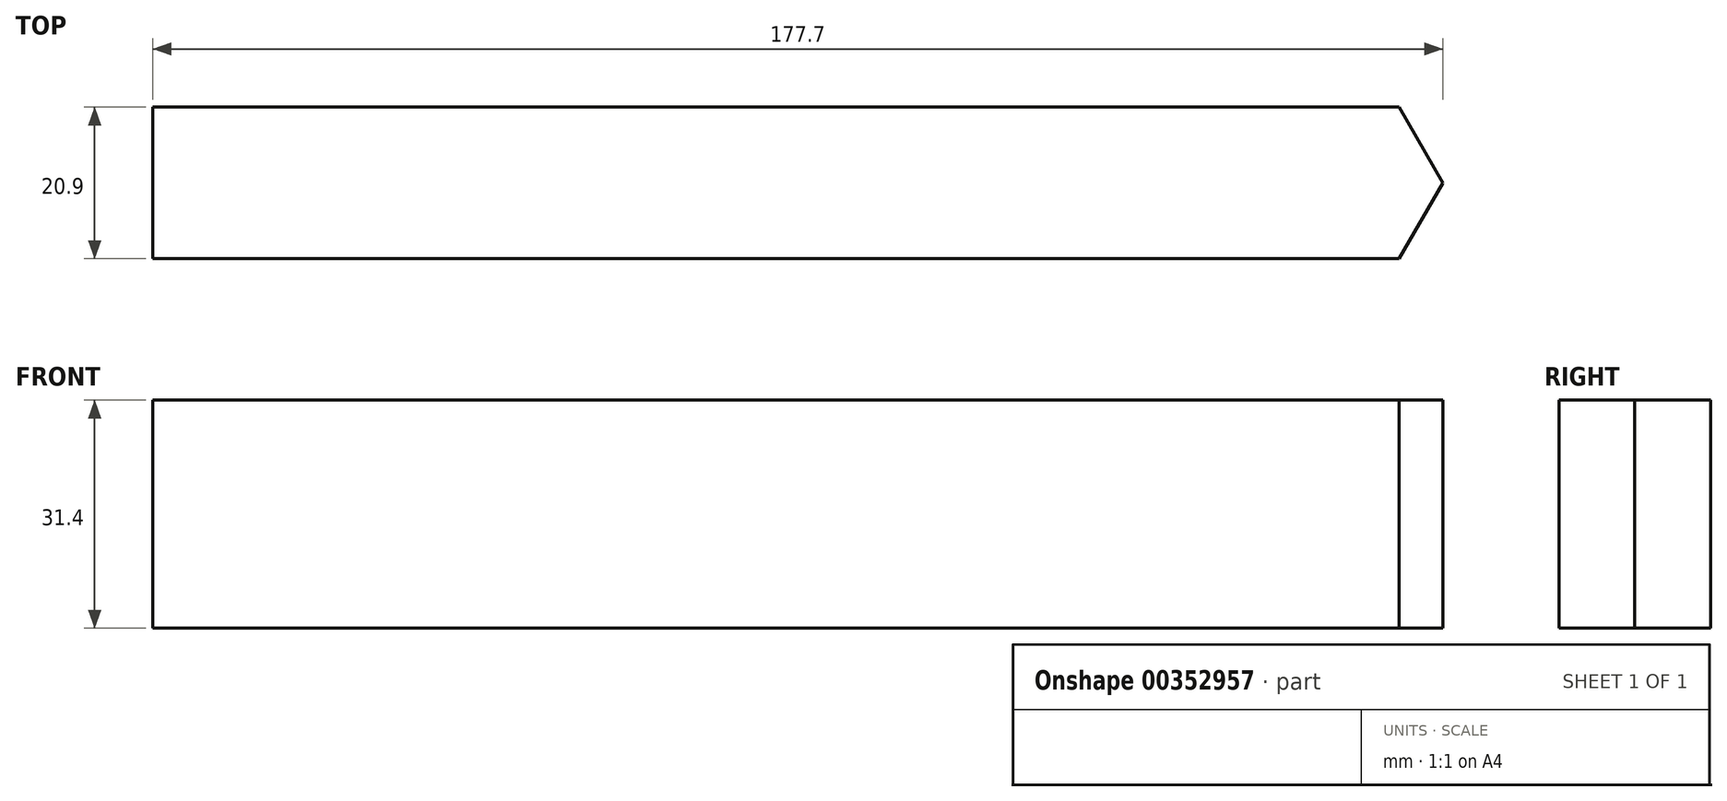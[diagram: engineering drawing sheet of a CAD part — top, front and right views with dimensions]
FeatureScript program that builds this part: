
annotation { "Feature Type Name" : "Feature", "Feature Type Description" : "" }
export const myFeature = defineFeature(function(context is Context, id is Id, definition is map)
    precondition{}
    {
        {
            var Q0;
            Q0=qCreatedBy(makeId("Top.planeOp"),FACE);
            var sketch = newSketch(context, id + "F0", { "sketchPlane" : qUnion([Q0])});
            skLineSegment(sketch, "E0.bottom", {"start": v(-132.89, -10.45) * mm, "end": v(38.81, -10.45) * mm});
            skLineSegment(sketch, "E0.top", {"start": v(-132.89, 10.45) * mm, "end": v(38.81, 10.45) * mm});
            skLineSegment(sketch, "E0.left", {"start": v(-132.89, -10.45) * mm, "end": v(-132.89, 10.45) * mm});
            skLineSegment(sketch, "E1", {"start": v(38.81, 10.45) * mm, "end": v(44.81, 0) * mm});
            skLineSegment(sketch, "E2", {"start": v(44.81, 0) * mm, "end": v(38.81, -10.45) * mm});
            skSolve(sketch);
        }
        {
            var Q0;
            Q0=qSketchRegion(id+"F0",true);
            var Q1;
            Q1=makeQuery(id+"F0.imprint","IMPRINT",FACE,{"disambiguationData":[TD([[makeQuery(id+"F0.imprint","IMPRINT",EDGE,{"derivedFrom":sQuery(id+"F0.wireOp",EDGE,"E0.bottom")}),1.0]])]});
            extrude(context, id + "F1", {"entities" : qUnion([Q0, Q1]), "depth" : 31.4 * mm});
        }
    });
